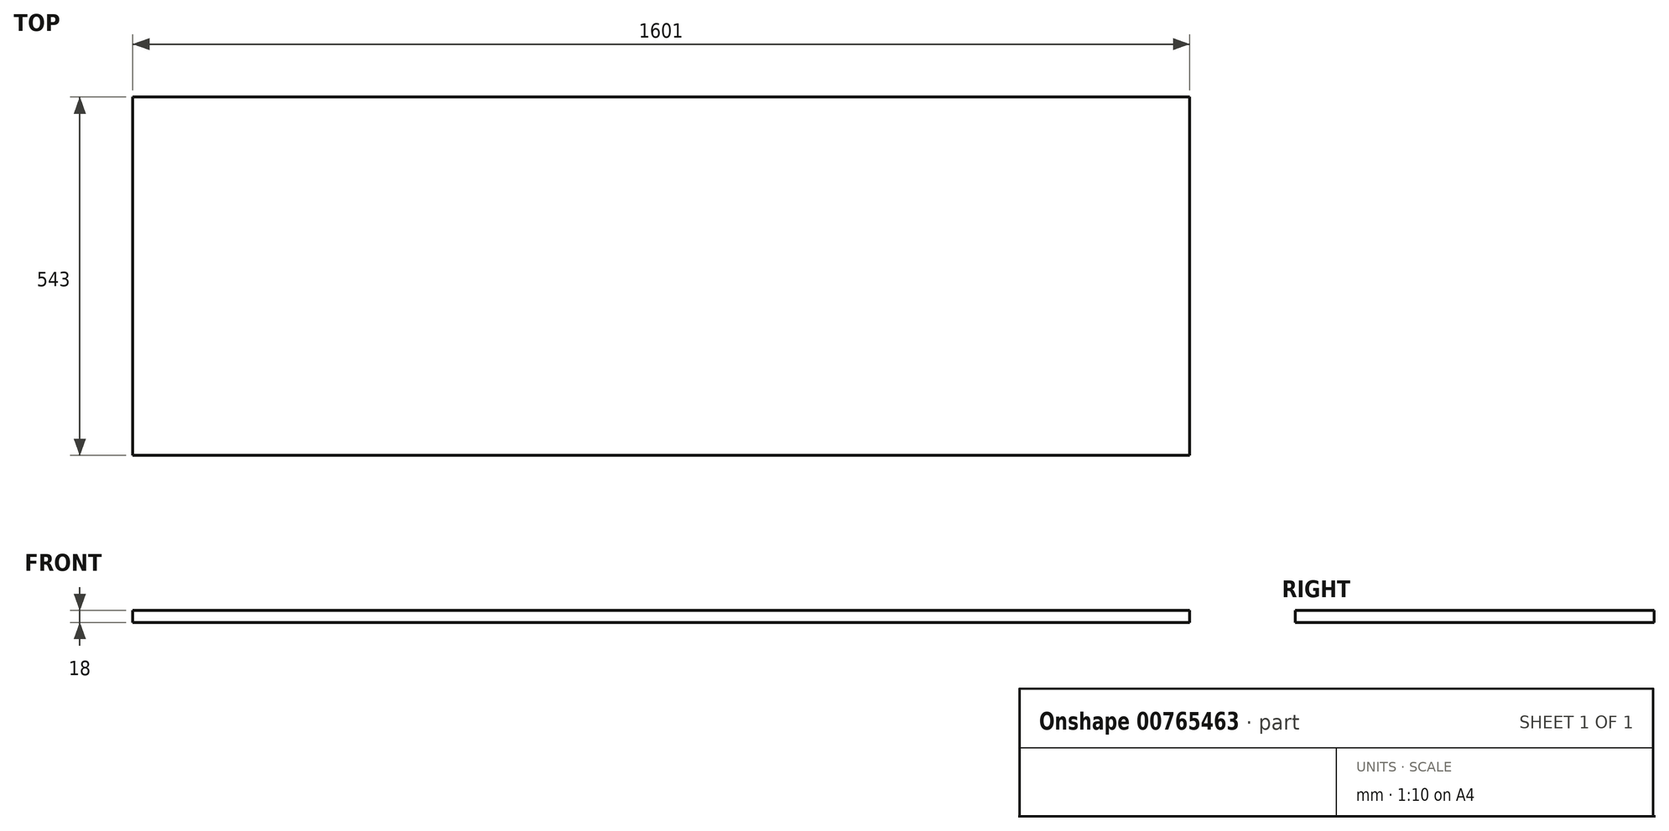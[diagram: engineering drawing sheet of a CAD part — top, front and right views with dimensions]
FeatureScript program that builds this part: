
annotation { "Feature Type Name" : "Feature", "Feature Type Description" : "" }
export const myFeature = defineFeature(function(context is Context, id is Id, definition is map)
    precondition{}
    {
        {
            var Q0;
            Q0=qCreatedBy(makeId("Top.planeOp"),FACE);
            var sketch = newSketch(context, id + "F0", { "sketchPlane" : qUnion([Q0])});
            skLineSegment(sketch, "E0.bottom", {"start": v(-800.5, -271.5) * mm, "end": v(800.5, -271.5) * mm});
            skLineSegment(sketch, "E0.top", {"start": v(-800.5, 271.5) * mm, "end": v(800.5, 271.5) * mm});
            skLineSegment(sketch, "E0.left", {"start": v(-800.5, -271.5) * mm, "end": v(-800.5, 271.5) * mm});
            skLineSegment(sketch, "E0.right", {"start": v(800.5, -271.5) * mm, "end": v(800.5, 271.5) * mm});
            skPoint(sketch, "E0.middle", {"position": v(0, 0) * mm});
            skSolve(sketch);
        }
        {
            var Q0;
            Q0 = qSketchRegion(id + "F0", true);
            extrude(context, id + "F1", {"entities" : qUnion([Q0]), "depth" : 18 * mm, "offsetDistance" : 25 * mm});
        }
    });
